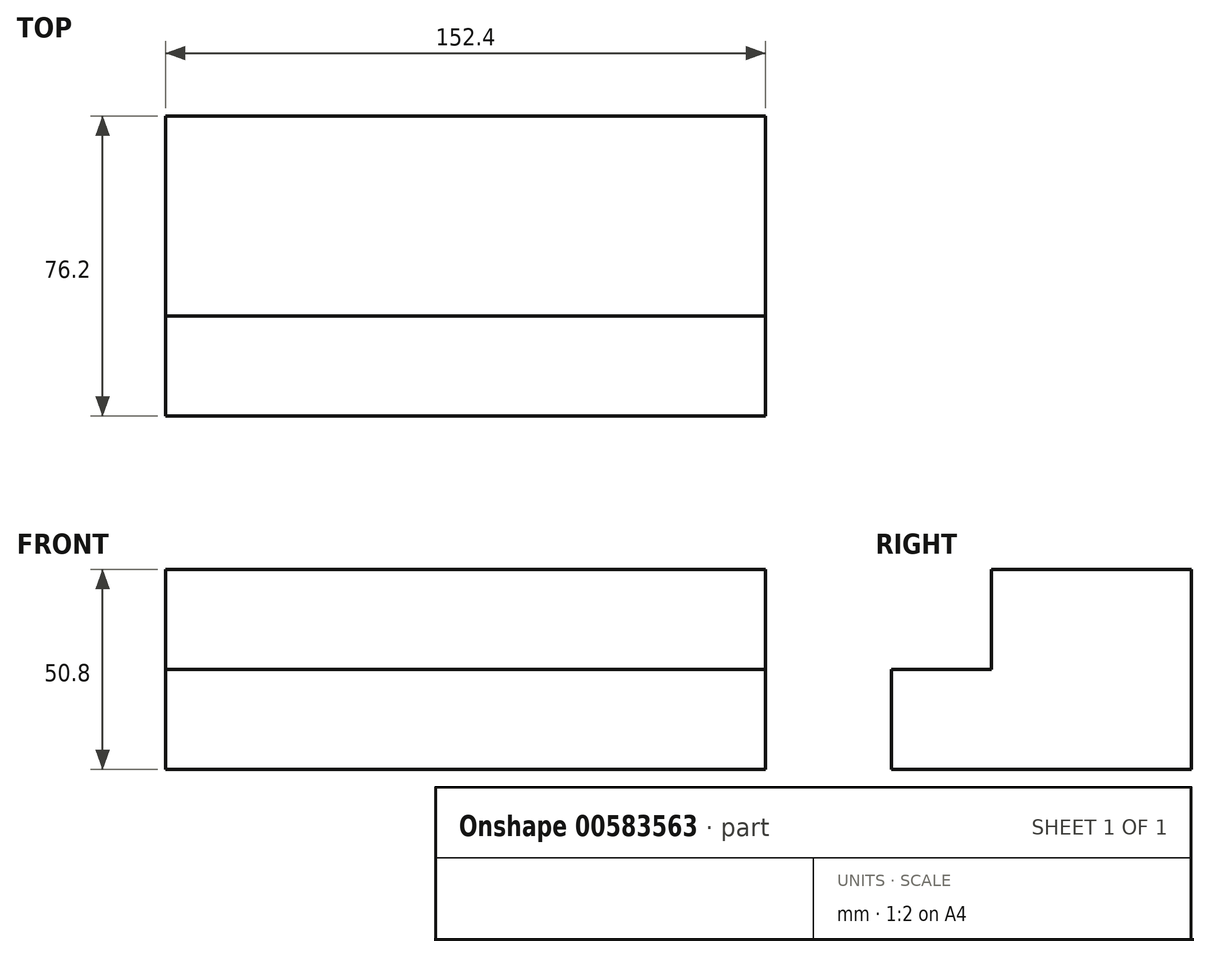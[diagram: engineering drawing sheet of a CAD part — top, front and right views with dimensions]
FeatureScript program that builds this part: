
annotation { "Feature Type Name" : "Feature", "Feature Type Description" : "" }
export const myFeature = defineFeature(function(context is Context, id is Id, definition is map)
    precondition{}
    {
        {
            var Q0;
            Q0=qCreatedBy(makeId("Right.planeOp"),FACE);
            var sketch = newSketch(context, id + "F0", { "sketchPlane" : qUnion([Q0])});
            skLineSegment(sketch, "E0", {"start": v(0, 0) * mm, "end": v(0, 25.4) * mm});
            skLineSegment(sketch, "E1", {"start": v(0, 25.4) * mm, "end": v(25.4, 25.4) * mm});
            skLineSegment(sketch, "E2", {"start": v(25.4, 25.4) * mm, "end": v(25.4, 50.8) * mm});
            skLineSegment(sketch, "E3", {"start": v(25.4, 50.8) * mm, "end": v(76.2, 50.8) * mm});
            skLineSegment(sketch, "E4", {"start": v(76.2, 50.8) * mm, "end": v(76.2, 0) * mm});
            skLineSegment(sketch, "E5", {"start": v(76.2, 0) * mm, "end": v(0, 0) * mm});
            skSolve(sketch);
        }
        {
            var Q0;
            Q0 = qSketchRegion(id + "F0", true);
            extrude(context, id + "F1", {"entities" : qUnion([Q0]), "depth" : 152.4 * mm, "offsetDistance" : 25.4 * mm});
        }
    });
